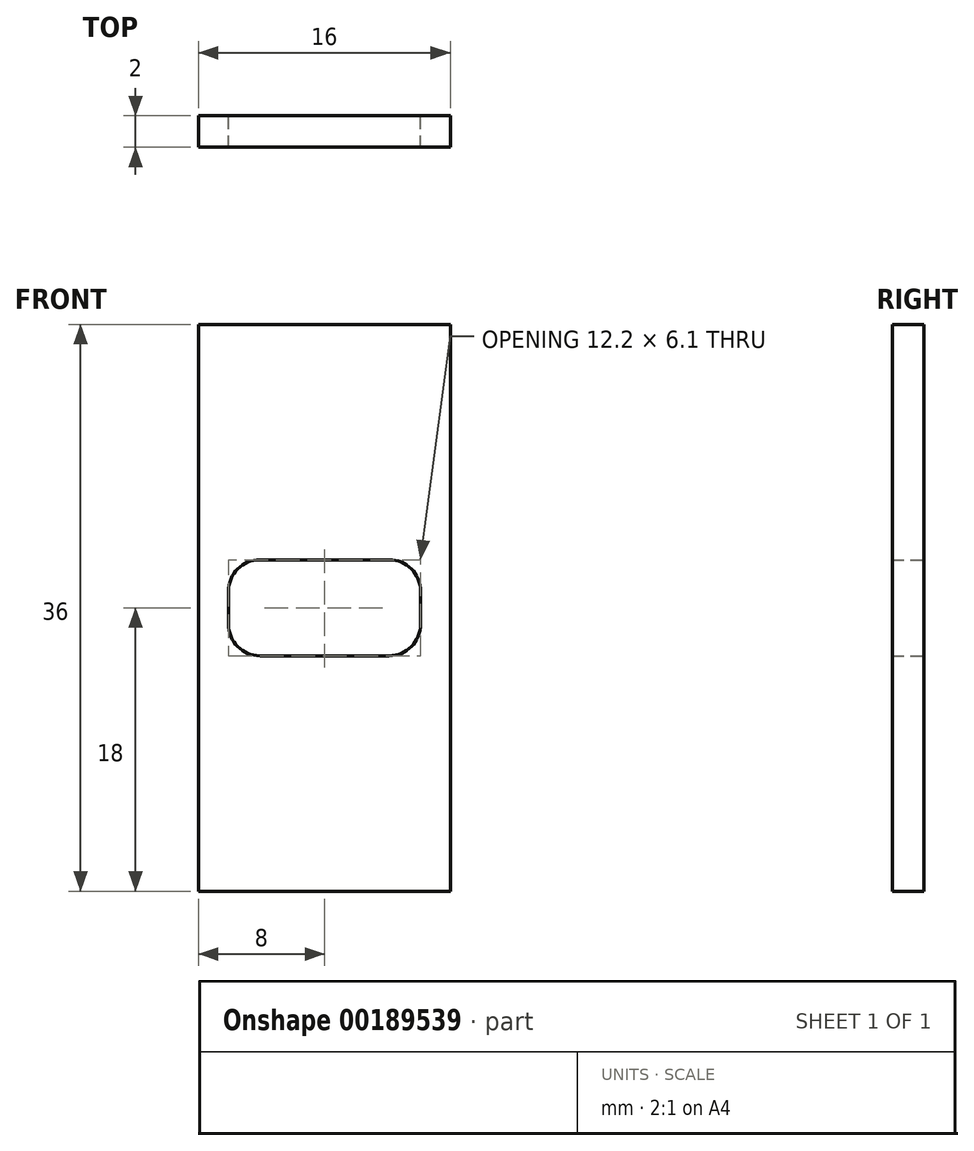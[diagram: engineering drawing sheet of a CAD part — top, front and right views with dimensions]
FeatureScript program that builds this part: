
annotation { "Feature Type Name" : "Feature", "Feature Type Description" : "" }
export const myFeature = defineFeature(function(context is Context, id is Id, definition is map)
    precondition{}
    {
        {
            var Q0;
            Q0=qCreatedBy(makeId("Front.planeOp"),FACE);
            var sketch = newSketch(context, id + "F0", { "sketchPlane" : qUnion([Q0])});
            skLineSegment(sketch, "E0.bottom", {"start": v(-8, 18) * mm, "end": v(8, 18) * mm});
            skLineSegment(sketch, "E0.top", {"start": v(-8, -18) * mm, "end": v(8, -18) * mm});
            skLineSegment(sketch, "E0.left", {"start": v(-8, 18) * mm, "end": v(-8, -18) * mm});
            skLineSegment(sketch, "E0.right", {"start": v(8, 18) * mm, "end": v(8, -18) * mm});
            skLineSegment(sketch, "E1.bottom", {"start": v(-6.1, 3.05) * mm, "end": v(6.1, 3.05) * mm});
            skLineSegment(sketch, "E1.top", {"start": v(-6.1, -3.05) * mm, "end": v(6.1, -3.05) * mm});
            skLineSegment(sketch, "E1.left", {"start": v(-6.1, 3.05) * mm, "end": v(-6.1, -3.05) * mm});
            skLineSegment(sketch, "E1.right", {"start": v(6.1, 3.05) * mm, "end": v(6.1, -3.05) * mm});
            skSolve(sketch);
        }
        {
            var Q0;
            Q0 = qSketchRegion(id + "F0", true);
            extrude(context, id + "F1", {"entities" : qUnion([Q0]), "depth" : 2 * mm});
        }
        {
            var Q0;
            Q0=makeQuery(id+"F1.opExtrude","SWEPT_EDGE",EDGE,{"disambiguationData":[OSD([sQuery(id+"F0.wireOp",EDGE,"E1.top"),sQuery(id+"F0.wireOp",EDGE,"E1.left")])]});
            var Q1;
            Q1=makeQuery(id+"F1.opExtrude","SWEPT_EDGE",EDGE,{"disambiguationData":[OSD([sQuery(id+"F0.wireOp",EDGE,"E1.bottom"),sQuery(id+"F0.wireOp",EDGE,"E1.left")])]});
            var Q2;
            Q2=makeQuery(id+"F1.opExtrude","SWEPT_EDGE",EDGE,{"disambiguationData":[OSD([sQuery(id+"F0.wireOp",EDGE,"E1.bottom"),sQuery(id+"F0.wireOp",EDGE,"E1.right")])]});
            var Q3;
            Q3=makeQuery(id+"F1.opExtrude","SWEPT_EDGE",EDGE,{"disambiguationData":[OSD([sQuery(id+"F0.wireOp",EDGE,"E1.top"),sQuery(id+"F0.wireOp",EDGE,"E1.right")])]});
            fillet(context, id + "F2", {"entities" : qUnion([Q0, Q1, Q2, Q3]), "radius" : 2 * mm, "tangentPropagation" : true, "allowEdgeOverflow" : false});
        }
    });
